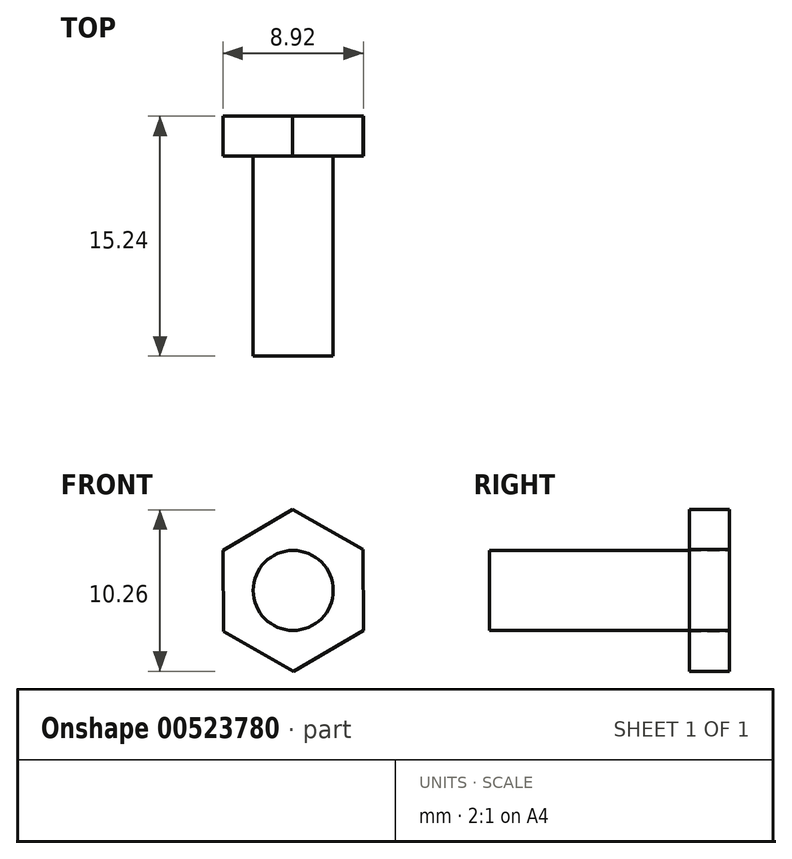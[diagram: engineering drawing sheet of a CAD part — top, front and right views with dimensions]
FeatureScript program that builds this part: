
annotation { "Feature Type Name" : "Feature", "Feature Type Description" : "" }
export const myFeature = defineFeature(function(context is Context, id is Id, definition is map)
    precondition{}
    {
        {
            var Q0;
            Q0=qCreatedBy(makeId("Front.planeOp"),FACE);
            var sketch = newSketch(context, id + "F0", { "sketchPlane" : qUnion([Q0])});
            skCircle(sketch, "E0.cCircle", {"center": v(0, 0) * mm, "radius": 4.45 * mm, "construction": true});
            skLineSegment(sketch, "E0.0", {"start": v(-0.03, 5.13) * mm, "end": v(4.43, 2.6) * mm});
            skLineSegment(sketch, "E0.1", {"start": v(4.43, 2.6) * mm, "end": v(4.46, -2.54) * mm});
            skLineSegment(sketch, "E0.2", {"start": v(4.46, -2.54) * mm, "end": v(0.03, -5.13) * mm});
            skLineSegment(sketch, "E0.3", {"start": v(0.03, -5.13) * mm, "end": v(-4.43, -2.6) * mm});
            skLineSegment(sketch, "E0.4", {"start": v(-4.43, -2.6) * mm, "end": v(-4.46, 2.54) * mm});
            skLineSegment(sketch, "E0.5", {"start": v(-4.46, 2.54) * mm, "end": v(-0.03, 5.13) * mm});
            skPoint(sketch, "E0.0.midPoint", {"position": v(2.2, 3.86) * mm});
            skSolve(sketch);
        }
        {
            var Q0;
            Q0=makeQuery(id+"F0.imprint","IMPRINT",FACE,{"disambiguationData":[TD([[makeQuery(id+"F0.imprint","IMPRINT",EDGE,{"derivedFrom":sQuery(id+"F0.wireOp",EDGE,"E0.0")}),-1.0]])]});
            extrude(context, id + "F1", {"entities" : qUnion([Q0]), "depth" : 2.54 * mm, "offsetDistance" : 25.4 * mm});
        }
        {
            var Q0;
            Q0=makeQuery(id+"F1.opExtrude","CAP_FACE",FACE,{"disambiguationData":[OSD([sQuery(id+"F0.wireOp",EDGE,"E0.0"),sQuery(id+"F0.wireOp",EDGE,"E0.1"),sQuery(id+"F0.wireOp",EDGE,"E0.2"),sQuery(id+"F0.wireOp",EDGE,"E0.3"),sQuery(id+"F0.wireOp",EDGE,"E0.4"),sQuery(id+"F0.wireOp",EDGE,"E0.5")])],"isStart":false});
            var sketch = newSketch(context, id + "F2", { "sketchPlane" : qUnion([Q0])});
            skCircle(sketch, "E1", {"center": v(0, 0) * mm, "radius": 2.54 * mm});
            skSolve(sketch);
        }
        {
            var Q0;
            Q0=makeQuery(id+"F2.imprint","IMPRINT",FACE,{"disambiguationData":[TD([[makeQuery(id+"F2.imprint","IMPRINT",EDGE,{"derivedFrom":sQuery(id+"F2.wireOp",EDGE,"E1")}),1.0]])]});
            extrude(context, id + "F3", {"entities" : qUnion([Q0]), "operationType" : NewBodyOperationType.ADD, "depth" : 12.7 * mm, "offsetDistance" : 25.4 * mm});
        }
    });
